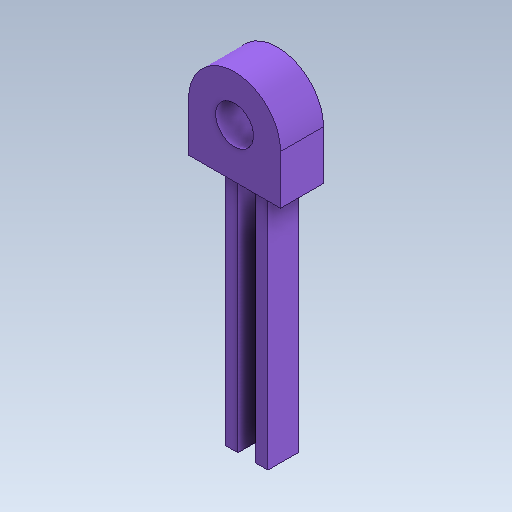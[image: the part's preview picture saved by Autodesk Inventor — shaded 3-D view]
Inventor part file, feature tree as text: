
AUTODESK INVENTOR PART (.ipt)
format: ipt  version: 2020 (Build 240168000, 168)  size: 226,304 bytes
history: native  units: in
note: dims shown in document units (in); Inventor stores cm internally (conversion verified against a paired STEP export)
features: extrude x8, sketch x8, projected_geometry x8
ambient origin geometry x8: Origin, YZ Plane, XZ Plane, XY Plane, X Axis, Y Axis, Z Axis, Center Point
bodies: Solid1 (feature_tree)
feature tree (24):
  extrude  "Extrusion1"  Depth=0.1358in
  extrude  "Extrusion4"  Depth=0.2894in
  extrude  "Extrusion5"  Depth=0.1378in TaperAngle=0.0deg
  extrude  "Extrusion6"  Depth=0.0797in
  extrude  "Extrusion7"  Depth=0.2953in
  extrude  "Extrusion8"  Depth=0.0787in TaperAngle=0.0deg
  extrude  "Extrusion9"  Depth=0.0394in
  extrude  "Extrusion11"  Depth=0.0394in TaperAngle=0.0deg
  sketch  "Sketch1"  dims[d0=0.7874in d1=0.1358in]
  sketch  "Sketch4"  dims[d2=0.1457in d3=0.2894in]
  projected_geometry  "Projected Loop3"
  sketch  "Sketch5"  dims[d4=0.1969in d5=0.1378in d6=0.0in]
  projected_geometry  "Projected Loop4"
  sketch  "Sketch6"  dims[d22=0.0797in d23=0.0797in]
  projected_geometry  "Projected Loop5"
  sketch  "Sketch7"  dims[d24=0.2953in d25=0.1575in]
  projected_geometry  "Projected Loop6"
  sketch  "Sketch8"  dims[d26=0.122in d27=0.0787in d28=0.0in]
  projected_geometry  "Projected Loop7"
  sketch  "Sketch9"  dims[d31=0.0394in d32=0.0394in]
  projected_geometry  "Projected Loop8"
  projected_geometry  "Projected Loop9"
  sketch  "Sketch11"  dims[d33=0.0689in d34=0.0in d35=0.0689in d36=0.0in d37=0.0197in d38=0.3937in d39=0.0in d40=0.7874in d41=0.0in d42=0.7874in d43=0.0in d46=0.0394in d47=0.0in]
  projected_geometry  "Projected Loop11"
